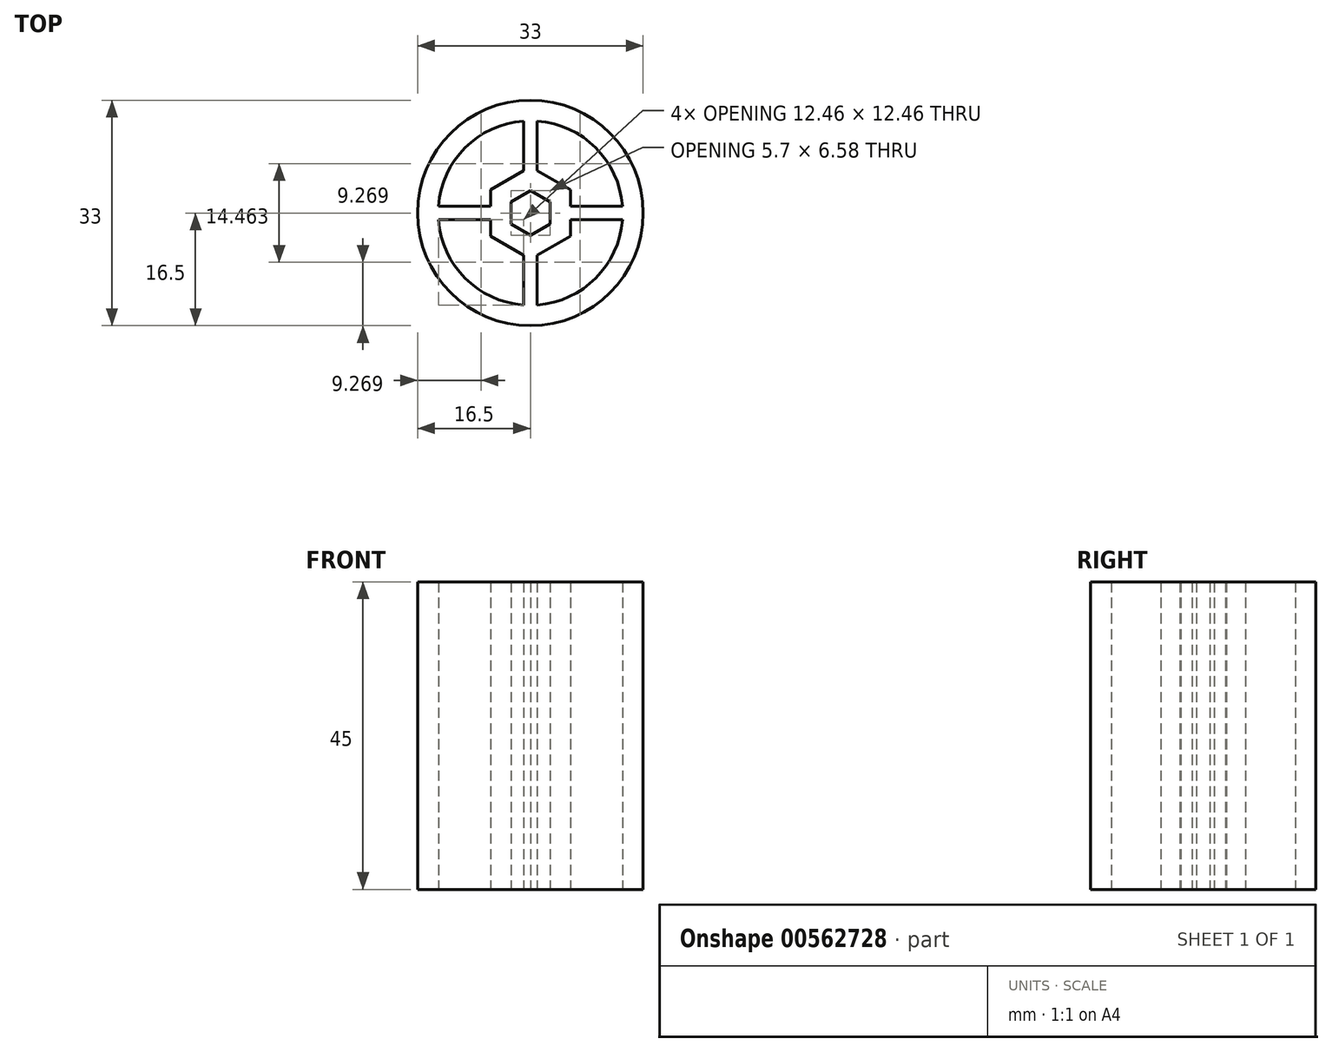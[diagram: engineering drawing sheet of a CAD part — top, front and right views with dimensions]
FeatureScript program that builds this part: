
annotation { "Feature Type Name" : "Feature", "Feature Type Description" : "" }
export const myFeature = defineFeature(function(context is Context, id is Id, definition is map)
    precondition{}
    {
        {
            var Q0;
            Q0=qCreatedBy(makeId("Top.planeOp"),FACE);
            var sketch = newSketch(context, id + "F0", { "sketchPlane" : qUnion([Q0])});
            skCircle(sketch, "E0", {"center": v(0, 0) * mm, "radius": 16.5 * mm});
            skSolve(sketch);
        }
        {
            var Q0;
            Q0 = qSketchRegion(id + "F0", true);
            extrude(context, id + "F1", {"entities" : qUnion([Q0]), "depth" : 45 * mm, "offsetDistance" : 25 * mm});
        }
        {
            var Q0;
            Q0=makeQuery(id+"F1.opExtrude","CAP_FACE",FACE,{"disambiguationData":[OSD([sQuery(id+"F0.wireOp",EDGE,"E0")])],"isStart":true});
            var sketch = newSketch(context, id + "F2", { "sketchPlane" : qUnion([Q0])});
            skCircle(sketch, "E1.cCircle", {"center": v(0, 0) * mm, "radius": 2.85 * mm, "construction": true});
            skLineSegment(sketch, "E1.0", {"start": v(2.85, 1.65) * mm, "end": v(2.85, -1.65) * mm});
            skLineSegment(sketch, "E1.1", {"start": v(2.85, -1.65) * mm, "end": v(0, -3.3) * mm});
            skLineSegment(sketch, "E1.2", {"start": v(0, -3.3) * mm, "end": v(-2.85, -1.65) * mm});
            skLineSegment(sketch, "E1.3", {"start": v(-2.85, -1.65) * mm, "end": v(-2.85, 1.65) * mm});
            skLineSegment(sketch, "E1.4", {"start": v(-2.85, 1.65) * mm, "end": v(0, 3.3) * mm});
            skLineSegment(sketch, "E1.5", {"start": v(0, 3.3) * mm, "end": v(2.85, 1.65) * mm});
            skPoint(sketch, "E1.0.midPoint", {"position": v(2.85, 0) * mm});
            skLineSegment(sketch, "E2.0", {"start": v(-5.85, -3.38) * mm, "end": v(-5.85, 3.38) * mm});
            skLineSegment(sketch, "E2.1", {"start": v(0, 6.75) * mm, "end": v(5.85, 3.38) * mm});
            skLineSegment(sketch, "E2.2", {"start": v(5.85, 3.38) * mm, "end": v(5.85, -3.38) * mm});
            skLineSegment(sketch, "E2.3", {"start": v(-5.85, 3.38) * mm, "end": v(0, 6.75) * mm});
            skLineSegment(sketch, "E2.4", {"start": v(5.85, -3.38) * mm, "end": v(0, -6.75) * mm});
            skLineSegment(sketch, "E2.5", {"start": v(0, -6.75) * mm, "end": v(-5.85, -3.38) * mm});
            skCircle(sketch, "E3.0", {"center": v(0, 0) * mm, "radius": 13.5 * mm});
            skLineSegment(sketch, "E4", {"start": v(-5.85, 1) * mm, "end": v(-13.46, 1) * mm});
            skLineSegment(sketch, "E5", {"start": v(-5.85, -1) * mm, "end": v(-13.46, -1) * mm});
            skLineSegment(sketch, "E6", {"start": v(0, 9.7) * mm, "end": v(0, -8.2) * mm, "construction": true});
            skLineSegment(sketch, "E7.MirrorCS", {"start": v(5.85, 1) * mm, "end": v(13.46, 1) * mm});
            skLineSegment(sketch, "E8.MirrorCS", {"start": v(5.85, -1) * mm, "end": v(13.46, -1) * mm});
            skLineSegment(sketch, "E9", {"start": v(-1, -6.18) * mm, "end": v(-1, -13.46) * mm});
            skLineSegment(sketch, "E10", {"start": v(1, -6.18) * mm, "end": v(1, -13.46) * mm});
            skLineSegment(sketch, "E11.MirrorCS", {"start": v(-1, 6.18) * mm, "end": v(-1, 13.46) * mm});
            skLineSegment(sketch, "E12.MirrorCS", {"start": v(1, 6.18) * mm, "end": v(1, 13.46) * mm});
            skSolve(sketch);
        }
        {
            var Q0;
            {var subQ0=sQuery(id+"F2.wireOp",EDGE,"E5");Q0=makeQuery(id+"F2.imprint","IMPRINT",FACE,{"disambiguationData":[TD([[makeQuery(id+"F2.imprint","IMPRINT",EDGE,{"derivedFrom":subQ0}),1.0]])]});}
            var Q1;
            {var subQ0=sQuery(id+"F2.wireOp",EDGE,"E8.MirrorCS");Q1=makeQuery(id+"F2.imprint","IMPRINT",FACE,{"disambiguationData":[TD([[makeQuery(id+"F2.imprint","IMPRINT",EDGE,{"derivedFrom":subQ0}),-1.0]])]});}
            var Q2;
            {var subQ0=sQuery(id+"F2.wireOp",EDGE,"E4");Q2=makeQuery(id+"F2.imprint","IMPRINT",FACE,{"disambiguationData":[TD([[makeQuery(id+"F2.imprint","IMPRINT",EDGE,{"derivedFrom":subQ0}),-1.0]])]});}
            var Q3;
            {var subQ3=sQuery(id+"F2.wireOp",EDGE,"E7.MirrorCS");Q3=makeQuery(id+"F2.imprint","IMPRINT",FACE,{"disambiguationData":[TD([[makeQuery(id+"F2.imprint","IMPRINT",EDGE,{"derivedFrom":subQ3}),1.0]])]});}
            var Q4;
            Q4=makeQuery(id+"F2.imprint","IMPRINT",FACE,{"disambiguationData":[TD([[makeQuery(id+"F2.imprint","IMPRINT",EDGE,{"derivedFrom":sQuery(id+"F2.wireOp",EDGE,"E1.0")}),-1.0]])]});
            extrude(context, id + "F3", {"entities" : qUnion([Q0, Q1, Q2, Q3, Q4]), "operationType" : NewBodyOperationType.REMOVE, "oppositeDirection" : true, "depth" : 45 * mm, "offsetDistance" : 25 * mm});
        }
    });
